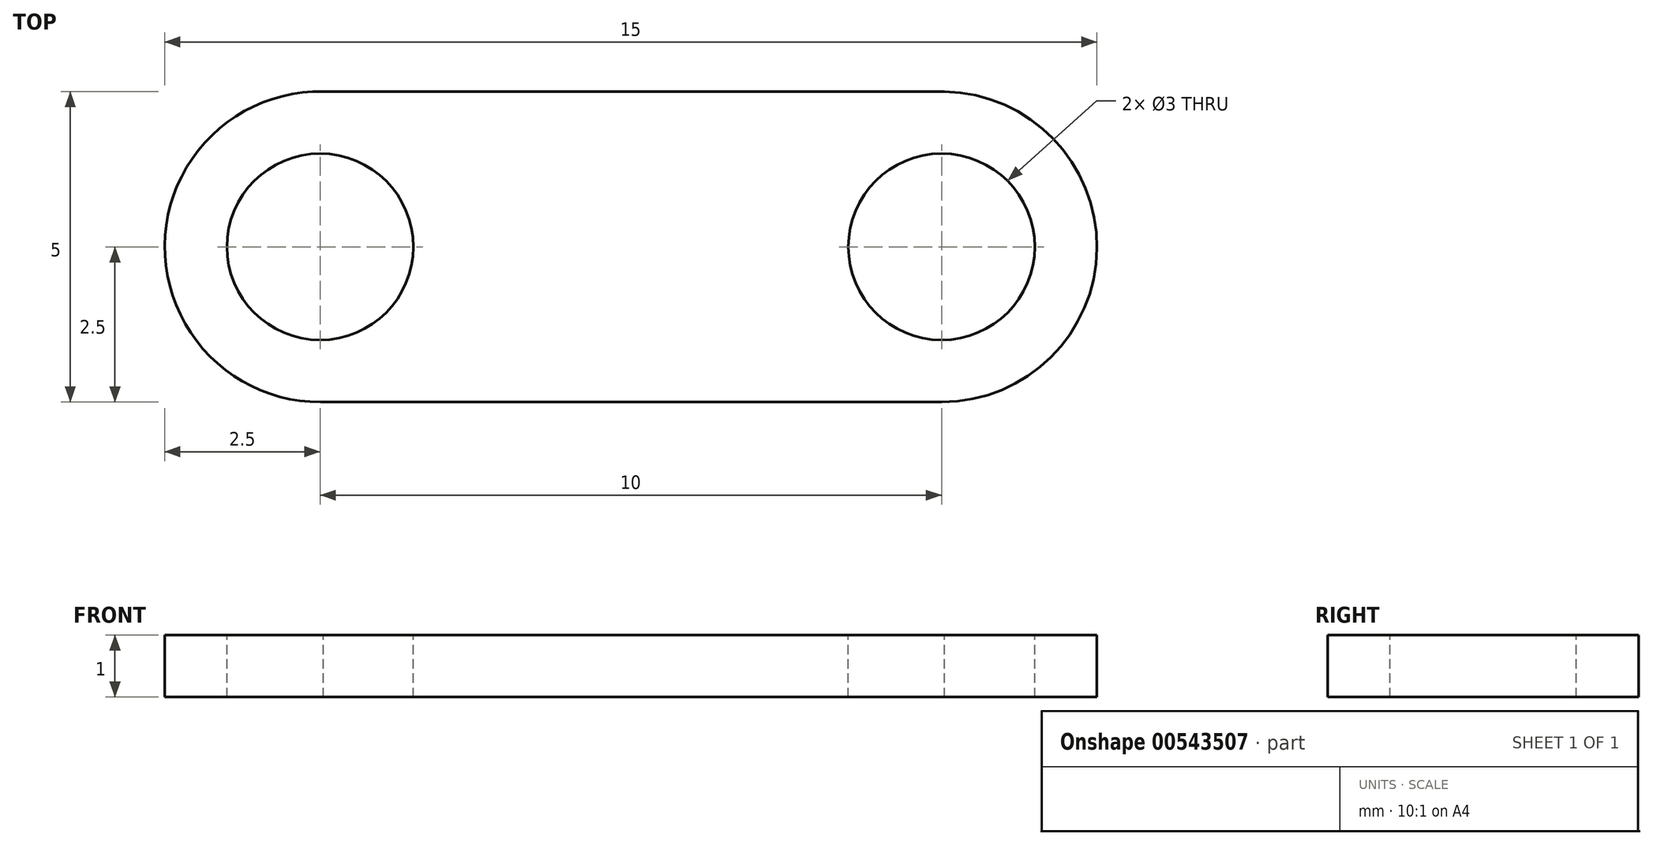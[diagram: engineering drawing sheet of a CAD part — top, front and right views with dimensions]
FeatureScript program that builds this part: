
annotation { "Feature Type Name" : "Feature", "Feature Type Description" : "" }
export const myFeature = defineFeature(function(context is Context, id is Id, definition is map)
    precondition{}
    {
        {
            var Q0;
            Q0=qCreatedBy(makeId("Top.planeOp"),FACE);
            var sketch = newSketch(context, id + "F0", { "sketchPlane" : qUnion([Q0])});
            skCircle(sketch, "E0", {"center": v(-5, 0) * mm, "radius": 1.5 * mm});
            skArc(sketch, "E1", {"start": v(-4.95, 2.5) * mm, "mid": v(-7.5, 0.02) * mm, "end": v(-5, -2.5) * mm});
            skCircle(sketch, "E2.MirrorC", {"center": v(5, 0) * mm, "radius": 1.5 * mm});
            skArc(sketch, "E3.MirrorC", {"start": v(4.95, 2.5) * mm, "mid": v(7.5, 0.02) * mm, "end": v(5, -2.5) * mm});
            skLineSegment(sketch, "E4", {"start": v(-5, -2.5) * mm, "end": v(5, -2.5) * mm});
            skLineSegment(sketch, "E5", {"start": v(-4.95, 2.5) * mm, "end": v(5.05, 2.5) * mm});
            skSolve(sketch);
        }
        {
            var Q0;
            Q0=makeQuery(id+"F0.imprint","IMPRINT",FACE,{"disambiguationData":[TD([[makeQuery(id+"F0.imprint","IMPRINT",EDGE,{"derivedFrom":sQuery(id+"F0.wireOp",EDGE,"E0")}),-1.0]])]});
            extrude(context, id + "F1", {"entities" : qUnion([Q0]), "oppositeDirection" : true, "depth" : 1 * mm, "offsetDistance" : 25.4 * mm});
        }
    });
